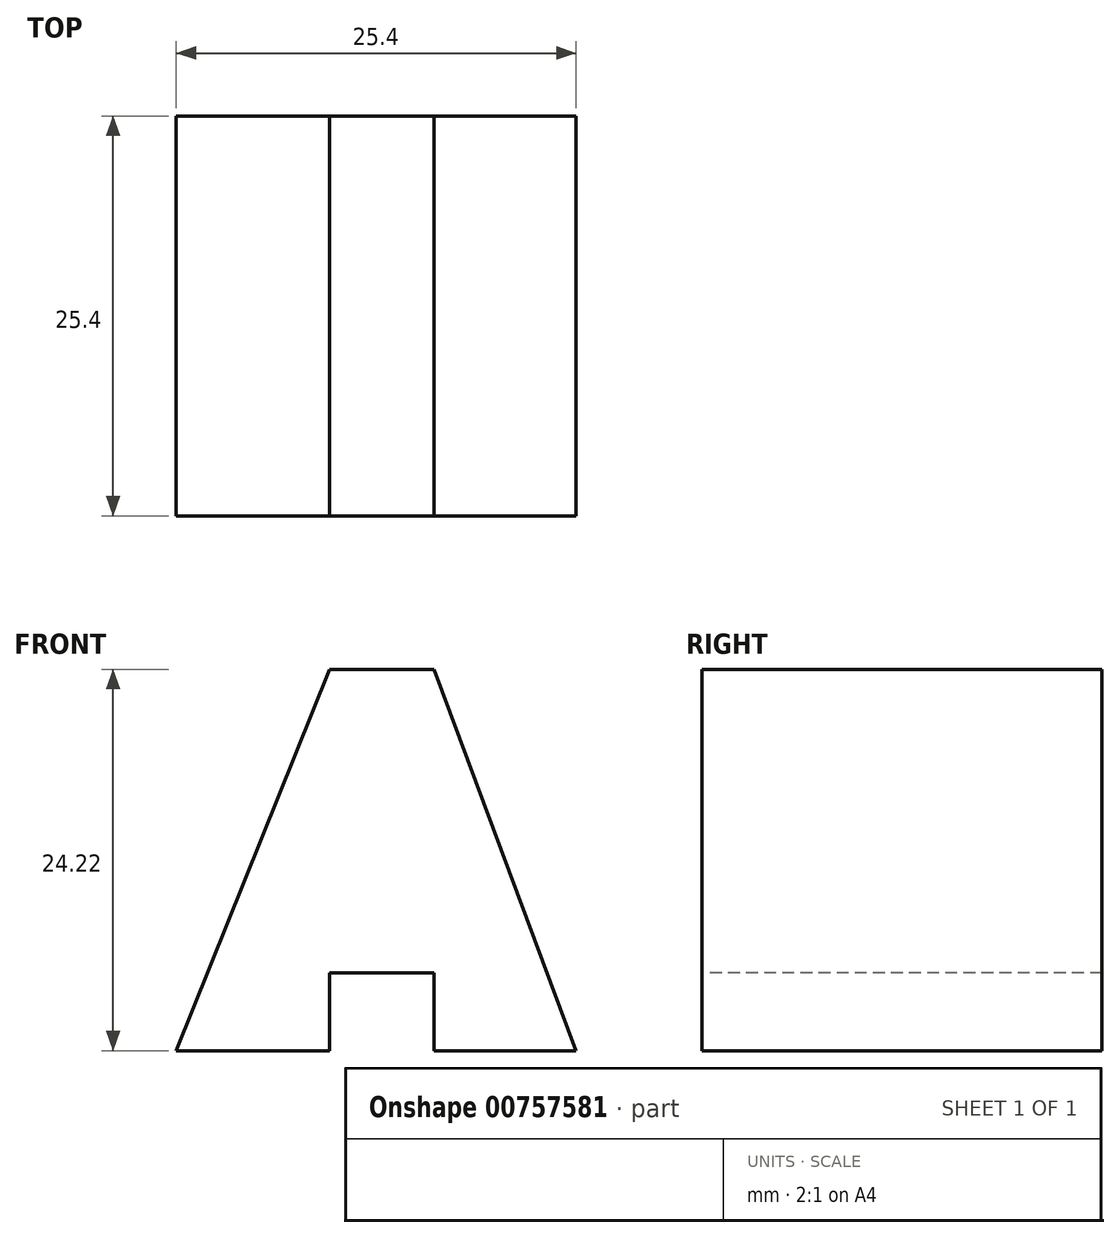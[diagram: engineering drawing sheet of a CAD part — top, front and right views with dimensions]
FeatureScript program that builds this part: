
annotation { "Feature Type Name" : "Feature", "Feature Type Description" : "" }
export const myFeature = defineFeature(function(context is Context, id is Id, definition is map)
    precondition{}
    {
        {
            var Q0;
            Q0=qCreatedBy(makeId("Front.planeOp"),FACE);
            var sketch = newSketch(context, id + "F0", { "sketchPlane" : qUnion([Q0])});
            skLineSegment(sketch, "E0", {"start": v(0, 31.75) * mm, "end": v(0, 0) * mm});
            skLineSegment(sketch, "E1", {"start": v(0, 0) * mm, "end": v(25.4, 0) * mm});
            skLineSegment(sketch, "E2", {"start": v(25.4, 0) * mm, "end": v(25.4, 31.75) * mm});
            skLineSegment(sketch, "E3", {"start": v(25.4, 31.75) * mm, "end": v(0, 31.75) * mm});
            skSolve(sketch);
        }
        {
            var Q0;
            Q0 = qSketchRegion(id + "F0", true);
            extrude(context, id + "F1", {"entities" : qUnion([Q0]), "depth" : 25.4 * mm, "offsetDistance" : 25.4 * mm});
        }
        {
            var Q0;
            Q0=makeQuery(id+"F1.opExtrude","CAP_FACE",FACE,{"disambiguationData":[OSD([sQuery(id+"F0.wireOp",EDGE,"E0"),sQuery(id+"F0.wireOp",EDGE,"E1"),sQuery(id+"F0.wireOp",EDGE,"E2"),sQuery(id+"F0.wireOp",EDGE,"E3")])],"isStart":false});
            var sketch = newSketch(context, id + "F2", { "sketchPlane" : qUnion([Q0])});
            skLineSegment(sketch, "E4", {"start": v(9.75, 0) * mm, "end": v(9.75, 4.93) * mm});
            skLineSegment(sketch, "E5", {"start": v(9.75, 4.93) * mm, "end": v(16.38, 4.93) * mm});
            skLineSegment(sketch, "E6", {"start": v(16.38, 4.93) * mm, "end": v(16.38, 0) * mm});
            skLineSegment(sketch, "E7", {"start": v(0, 0) * mm, "end": v(9.75, 24.22) * mm});
            skLineSegment(sketch, "E8", {"start": v(25.4, 0) * mm, "end": v(16.38, 24.22) * mm});
            skLineSegment(sketch, "E9", {"start": v(9.75, 24.22) * mm, "end": v(16.38, 24.22) * mm});
            skSolve(sketch);
        }
        {
            var Q0;
            {var subQ0=sQuery(id+"F2.wireOp",EDGE,"E4");Q0=makeQuery(id+"F2.imprint","IMPRINT",FACE,{"disambiguationData":[TD([[makeQuery(id+"F2.imprint","IMPRINT",EDGE,{"derivedFrom":subQ0}),-1.0]])]});}
            extrude(context, id + "F3", {"entities" : qUnion([Q0]), "operationType" : NewBodyOperationType.REMOVE, "endBound" : BoundingType.THROUGH_ALL, "oppositeDirection" : true, "depth" : 25.4 * mm, "offsetDistance" : 25.4 * mm});
        }
        {
            var Q0;
            Q0=makeQuery(id+"F2.imprint","IMPRINT",FACE,{"disambiguationData":[TD([[makeQuery(id+"F2.imprint","IMPRINT",EDGE,{"derivedFrom":sQuery(id+"F2.wireOp",EDGE,"E7")}),1.0]])]});
            var sketch = newSketch(context, id + "F4", { "sketchPlane" : qUnion([Q0])});
            skSolve(sketch);
        }
        {
            var Q0;
            Q0 = qSketchRegion(id + "F4", true);
            var Q1;
            Q1=makeQuery(id+"F4.imprint","IMPRINT",FACE,{"disambiguationData":[TD([[makeQuery(id+"F4.imprint","IMPRINT",EDGE,{"derivedFrom":makeQuery(id+"F2.imprint","IMPRINT",EDGE,{"derivedFrom":sQuery(id+"F2.wireOp",EDGE,"E7")})}),1.0]])]});
            extrude(context, id + "F5", {"entities" : qUnion([Q0, Q1]), "operationType" : NewBodyOperationType.REMOVE, "endBound" : BoundingType.THROUGH_ALL, "oppositeDirection" : true, "depth" : 25.4 * mm, "offsetDistance" : 25.4 * mm});
        }
        {
            var Q0;
            Q0=makeQuery(id+"F2.imprint","IMPRINT",FACE,{"disambiguationData":[TD([[makeQuery(id+"F2.imprint","IMPRINT",EDGE,{"derivedFrom":sQuery(id+"F2.wireOp",EDGE,"E7")}),1.0]])]});
            extrude(context, id + "F6", {"entities" : qUnion([Q0]), "operationType" : NewBodyOperationType.REMOVE, "endBound" : BoundingType.THROUGH_ALL, "oppositeDirection" : true, "depth" : 25.4 * mm, "offsetDistance" : 25.4 * mm});
        }
        {
            var Q0;
            Q0=makeQuery(id+"F2.imprint","IMPRINT",FACE,{"disambiguationData":[TD([[makeQuery(id+"F2.imprint","IMPRINT",EDGE,{"derivedFrom":sQuery(id+"F2.wireOp",EDGE,"E7")}),1.0]])]});
            extrude(context, id + "F7", {"entities" : qUnion([Q0]), "operationType" : NewBodyOperationType.REMOVE, "endBound" : BoundingType.THROUGH_ALL, "oppositeDirection" : true, "depth" : 25.4 * mm, "offsetDistance" : 25.4 * mm});
        }
    });
